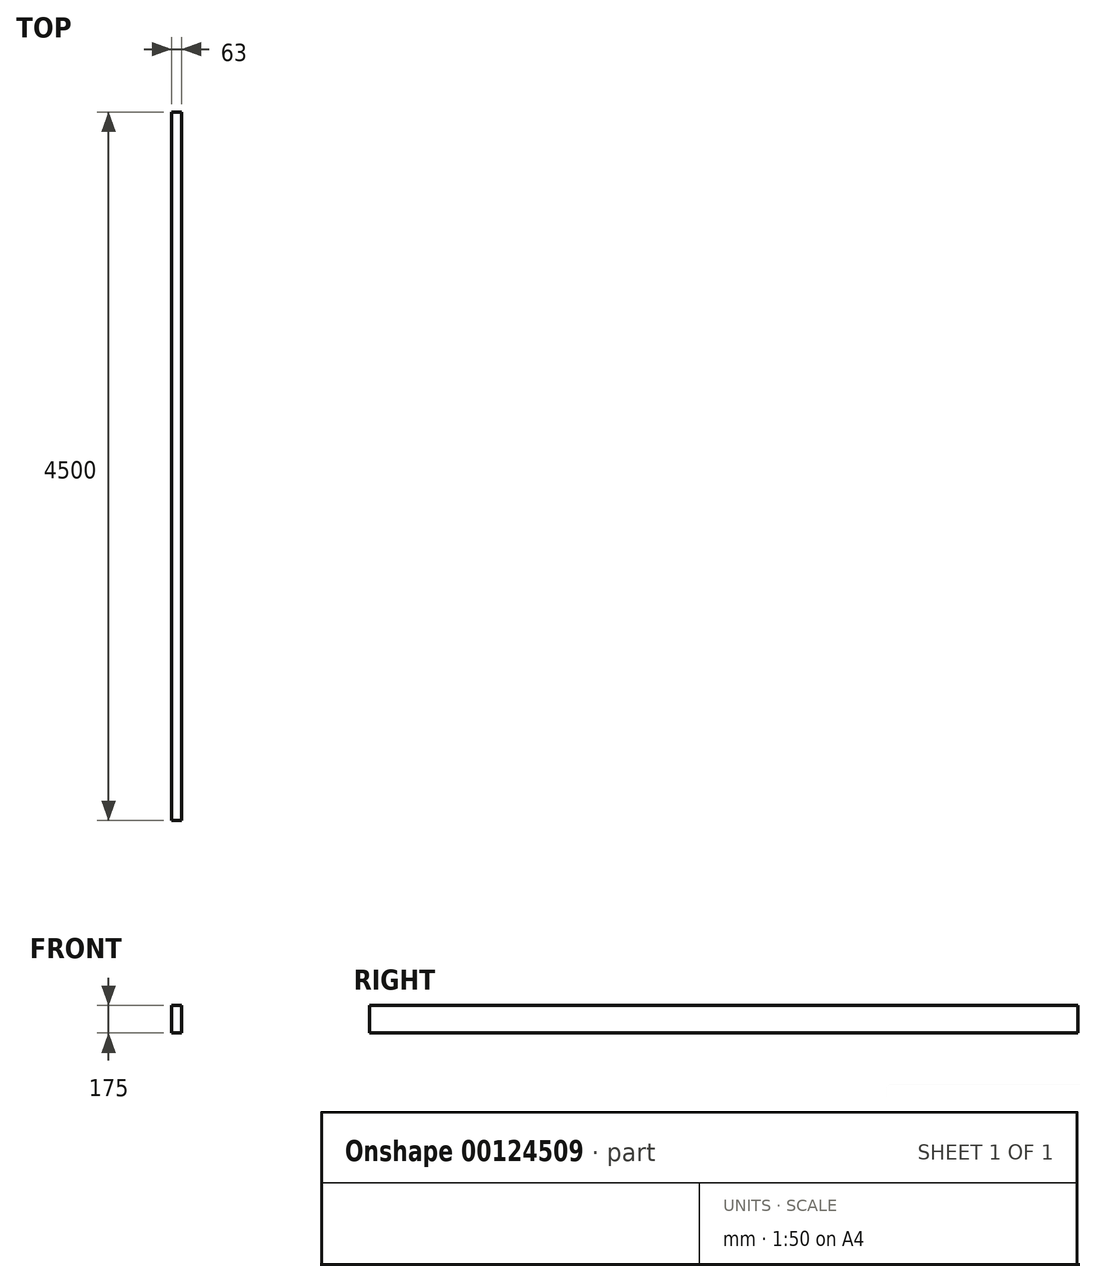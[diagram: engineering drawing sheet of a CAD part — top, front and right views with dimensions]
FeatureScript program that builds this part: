
annotation { "Feature Type Name" : "Feature", "Feature Type Description" : "" }
export const myFeature = defineFeature(function(context is Context, id is Id, definition is map)
    precondition{}
    {
        {
            var Q0;
            Q0=qCreatedBy(makeId("Front.planeOp"),FACE);
            var sketch = newSketch(context, id + "F0", { "sketchPlane" : qUnion([Q0])});
            skLineSegment(sketch, "E0.bottom", {"start": v(-28.95, 87.5) * mm, "end": v(34.05, 87.5) * mm});
            skLineSegment(sketch, "E0.top", {"start": v(-28.95, -87.5) * mm, "end": v(34.05, -87.5) * mm});
            skLineSegment(sketch, "E0.left", {"start": v(-28.95, 87.5) * mm, "end": v(-28.95, -87.5) * mm});
            skLineSegment(sketch, "E0.right", {"start": v(34.05, 87.5) * mm, "end": v(34.05, -87.5) * mm});
            skPoint(sketch, "E0.middle", {"position": v(2.55, 0) * mm});
            skSolve(sketch);
        }
        {
            var Q0;
            Q0 = qSketchRegion(id + "F0", true);
            extrude(context, id + "F1", {"entities" : qUnion([Q0]), "endBound" : BoundingType.SYMMETRIC, "depth" : 4500 * mm});
        }
    });
